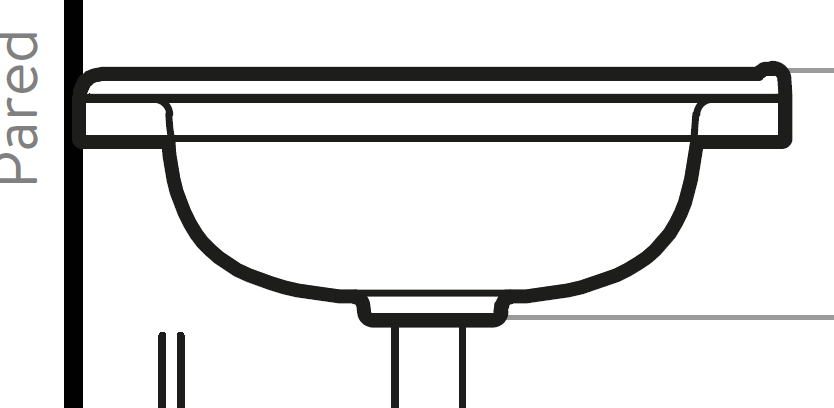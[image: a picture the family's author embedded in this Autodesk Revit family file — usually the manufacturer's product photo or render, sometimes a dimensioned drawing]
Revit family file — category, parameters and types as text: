
# Revit family: 603271711_Mueble aluvia Miel a Piso 40x35
name_source: partatom
category: Plumbing Fixtures
units: mm (PartAtom-declared; Revit-internal decimal feet)

## family parameters
Always vertical = Yes
Cut with Voids When Loaded = No
OmniClass Number = 23.31.13.11
OmniClass Title = Single Sinks
Part Type = Normal
Room Calculation Point = No
Round Connector Dimension = Use Diameter
Shared = No
Work Plane-Based = Yes

## types (2) — shared parameters
Alto = 850 mm  [stored 2.78871 ft]
Ancho = 395 mm  [stored 1.29593 ft]
Canto = PVC rígido 2 mm de calibre.
Carga máxima = 77,2 lb (35 kg).
Default Elevation = 1219 mm
Densidad = 15 mms 670 kg./m^3.
Description = La línea ALUVIA viene a entregar de manera asequible una solución perfecta que combina
diseño y funcionalidad, ALUVIA se inspira en el movimiento y caída del agua en la
naturaleza, es por ello de sus formas orgánicas donde podemos obtener un producto
compacto y de líneas fluidas, que se adapta en espacios pequeños.
el pricipal benefico de los muebles de esta linea es ser un producto compacto que cuenta
con cajón y repisa brindándole al consumidor mayor capacidad de almacenamiento,
brindando una excelente solución para aquellos espacios pequeños.
· Mueble compacto para espacios pequeños.
· Lavamanos 100% en porcelana.
· Grán capacidad de almacenamiento.
Dimensiones Generales (H * W * P) = 33,46” x 15,55” x 13,58” (850 x 395 x 345 mm).
Garantia Herrajes = 1 año
Garantia Madera = 1 año
Manufacturer = Corona
Material Lavamanos = Corona_Cerámica_Sinterizada
Material madera interior = Corona_Madera_Aglomerada_Plomo
Model = Mueble aluvia miel LVM 45X45
Patas = Corona_Acero
Peso Bruto aprox = 35,9 lb (16,3 kg).
Peso Neto aprox = 33,5 lb (15,2 kg).
Pieza en U = Corona_Poliestrieno_Gris
Profundidad = 350 mm  [stored 1.14829 ft]
Resistencia a la humedad = 8%
Resistencia al rayado = 700 ciclos
Textura = Habano: Poro - Gris: Soft
Miel:poro - Plomo:mate.

## per-type parameters (varying)
| type | Material | URL |
| Ref. 603271711 Mueble Aluvia Miel Con Lavamanos | Corona_Madera_Aglomerada_Miel | https://corona.co |
| Ref. 603276091 Mueble Aluvia Habano Con Lavamanos | Corona_Madera_Aglomerada_Habano |  |

note: [stored X ft] marks values corroborated as IEEE doubles in the binary element streams (Revit-internal decimal feet)

## geometry (parser evidence)
native form markers: Blend x4, Extrusion x1, Sweep x35
no freeform markers — native parametric forms only
